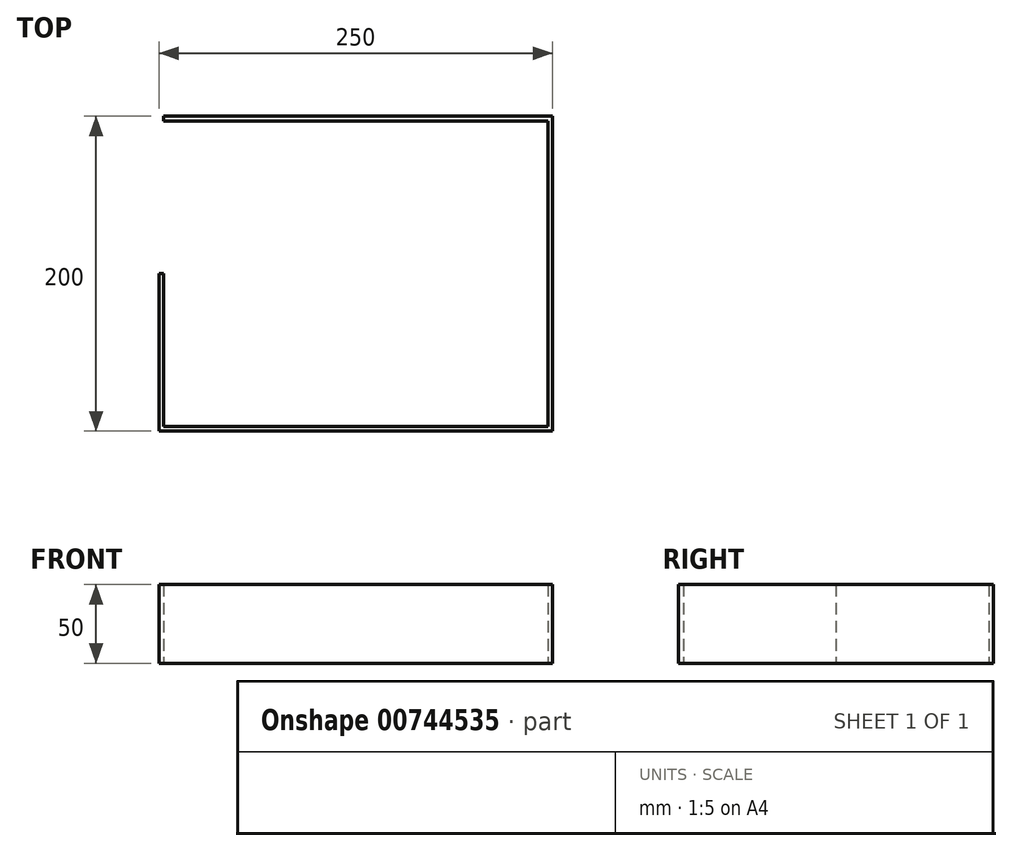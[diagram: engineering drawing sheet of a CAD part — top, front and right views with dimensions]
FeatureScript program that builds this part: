
annotation { "Feature Type Name" : "Feature", "Feature Type Description" : "" }
export const myFeature = defineFeature(function(context is Context, id is Id, definition is map)
    precondition{}
    {
        {
            var Q0;
            Q0=qCreatedBy(makeId("Top.planeOp"),FACE);
            var sketch = newSketch(context, id + "F0", { "sketchPlane" : qUnion([Q0])});
            skLineSegment(sketch, "E0.bottom", {"start": v(-125.37, 86.74) * mm, "end": v(124.63, 86.74) * mm});
            skLineSegment(sketch, "E0.top", {"start": v(-125.37, -113.26) * mm, "end": v(124.63, -113.26) * mm});
            skLineSegment(sketch, "E0.left", {"start": v(-125.37, 86.74) * mm, "end": v(-125.37, -113.26) * mm});
            skLineSegment(sketch, "E0.right", {"start": v(124.63, 86.74) * mm, "end": v(124.63, -113.26) * mm});
            skLineSegment(sketch, "E1", {"start": v(114.94, 86.74) * mm, "end": v(114.94, 83.74) * mm});
            skLineSegment(sketch, "E2", {"start": v(124.63, 83.74) * mm, "end": v(121.63, 83.74) * mm});
            skLineSegment(sketch, "E3", {"start": v(121.63, 83.74) * mm, "end": v(-125.37, 83.74) * mm});
            skLineSegment(sketch, "E4", {"start": v(-125.37, 83.74) * mm, "end": v(-122.37, 83.74) * mm});
            skLineSegment(sketch, "E5", {"start": v(-122.37, 83.74) * mm, "end": v(-122.37, 86.74) * mm});
            skLineSegment(sketch, "E6", {"start": v(-122.37, 86.74) * mm, "end": v(-122.37, -113.26) * mm});
            skLineSegment(sketch, "E7", {"start": v(-125.37, -113.26) * mm, "end": v(-125.37, -13.26) * mm});
            skLineSegment(sketch, "E8", {"start": v(-125.37, -13.26) * mm, "end": v(-110.07, -13.26) * mm});
            skLineSegment(sketch, "E9.MirrorCS", {"start": v(121.63, -110.26) * mm, "end": v(-125.37, -110.26) * mm});
            skLineSegment(sketch, "E10", {"start": v(-125.37, 86.74) * mm, "end": v(-0.37, 86.74) * mm});
            skLineSegment(sketch, "E11", {"start": v(-0.37, 86.74) * mm, "end": v(-0.37, 77.7) * mm});
            skLineSegment(sketch, "E12.MirrorCS", {"start": v(121.63, 86.74) * mm, "end": v(121.63, -113.26) * mm});
            skSolve(sketch);
        }
        {
            var Q0;
            {var subQ3=sQuery(id+"F0.wireOp",EDGE,"E4");Q0=makeQuery(id+"F0.imprint","IMPRINT",FACE,{"disambiguationData":[TD([[makeQuery(id+"F0.imprint","IMPRINT",EDGE,{"derivedFrom":subQ3}),-1.0]])]});}
            var Q1;
            {var subQ3=sQuery(id+"F0.wireOp",EDGE,"E4");Q1=makeQuery(id+"F0.imprint","IMPRINT",FACE,{"disambiguationData":[TD([[makeQuery(id+"F0.imprint","IMPRINT",EDGE,{"derivedFrom":subQ3}),1.0]])]});}
            var Q2;
            {var subQ1=sQuery(id+"F0.wireOp",EDGE,"E3");var subQ3=sQuery(id+"F0.wireOp",EDGE,"E11");var subQ4=makeQuery(id+"F0.imprint","INTERSECT",VERTEX,{"derivedFrom":[subQ1,subQ3]});Q2=makeQuery(id+"F0.imprint","IMPRINT",FACE,{"disambiguationData":[TD([[makeQuery(id+"F0.imprint","IMPRINT",EDGE,{"disambiguationData":[TD([[subQ4,-1.0]])],"derivedFrom":subQ1}),-1.0]])]});}
            var Q3;
            {var subQ3=sQuery(id+"F0.wireOp",EDGE,"E1");Q3=makeQuery(id+"F0.imprint","IMPRINT",FACE,{"disambiguationData":[TD([[makeQuery(id+"F0.imprint","IMPRINT",EDGE,{"derivedFrom":subQ3}),-1.0]])]});}
            var Q4;
            {var subQ0=sQuery(id+"F0.wireOp",EDGE,"E1");Q4=makeQuery(id+"F0.imprint","IMPRINT",FACE,{"disambiguationData":[TD([[makeQuery(id+"F0.imprint","IMPRINT",EDGE,{"derivedFrom":subQ0}),1.0]])]});}
            var Q5;
            {var subQ5=sQuery(id+"F0.wireOp",EDGE,"E2");Q5=makeQuery(id+"F0.imprint","IMPRINT",FACE,{"disambiguationData":[TD([[makeQuery(id+"F0.imprint","IMPRINT",EDGE,{"derivedFrom":subQ5}),-1.0]])]});}
            var Q6;
            {var subQ0=sQuery(id+"F0.wireOp",EDGE,"E2");Q6=makeQuery(id+"F0.imprint","IMPRINT",FACE,{"disambiguationData":[TD([[makeQuery(id+"F0.imprint","IMPRINT",EDGE,{"derivedFrom":subQ0}),1.0]])]});}
            var Q7;
            {var subQ0=sQuery(id+"F0.wireOp",EDGE,"E6");var subQ1=sQuery(id+"F0.wireOp",EDGE,"E0.top");var subQ2=makeQuery(id+"F0.imprint","INTERSECT",VERTEX,{"derivedFrom":[subQ1,subQ0]});Q7=makeQuery(id+"F0.imprint","IMPRINT",FACE,{"disambiguationData":[TD([[makeQuery(id+"F0.imprint","IMPRINT",EDGE,{"disambiguationData":[TD([[subQ2,-1.0]])],"derivedFrom":subQ1}),1.0]])]});}
            var Q8;
            {var subQ0=sQuery(id+"F0.wireOp",EDGE,"E8");var subQ1=sQuery(id+"F0.wireOp",EDGE,"E6");var subQ2=makeQuery(id+"F0.imprint","INTERSECT",VERTEX,{"derivedFrom":[subQ1,subQ0]});Q8=makeQuery(id+"F0.imprint","IMPRINT",FACE,{"disambiguationData":[TD([[makeQuery(id+"F0.imprint","IMPRINT",EDGE,{"disambiguationData":[TD([[subQ2,-1.0]])],"derivedFrom":subQ1}),-1.0]])]});}
            var Q9;
            {var subQ0=sQuery(id+"F0.wireOp",EDGE,"E7");var subQ1=sQuery(id+"F0.wireOp",EDGE,"E0.top");var subQ2=makeQuery(id+"F0.imprint","INTERSECT",VERTEX,{"derivedFrom":[subQ1,subQ0]});Q9=makeQuery(id+"F0.imprint","IMPRINT",FACE,{"disambiguationData":[TD([[makeQuery(id+"F0.imprint","IMPRINT",EDGE,{"disambiguationData":[TD([[subQ2,-1.0]])],"derivedFrom":subQ1}),1.0]])]});}
            extrude(context, id + "F1", {"entities" : qUnion([Q0, Q1, Q2, Q3, Q4, Q5, Q6, Q7, Q8, Q9]), "depth" : 50 * mm, "offsetDistance" : 25 * mm});
        }
    });
